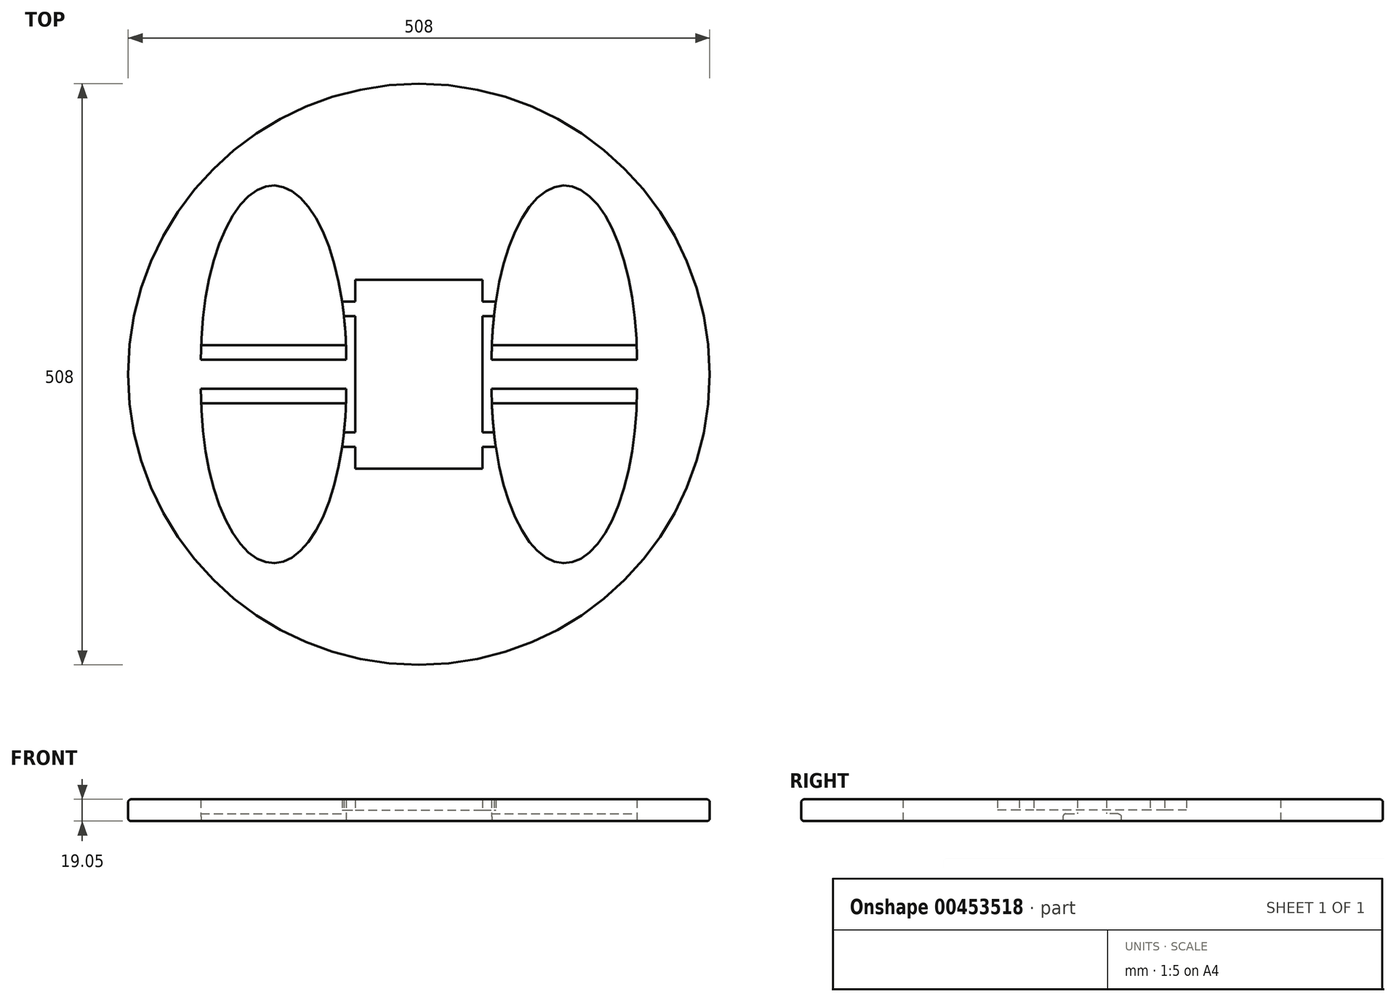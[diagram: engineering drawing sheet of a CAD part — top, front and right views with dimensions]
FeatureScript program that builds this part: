
annotation { "Feature Type Name" : "Feature", "Feature Type Description" : "" }
export const myFeature = defineFeature(function(context is Context, id is Id, definition is map)
    precondition{}
    {
        {
            var Q0;
            Q0=qCreatedBy(makeId("Top.planeOp"),FACE);
            var sketch = newSketch(context, id + "F0", { "sketchPlane" : qUnion([Q0])});
            skCircle(sketch, "E0", {"center": v(0, 0) * mm, "radius": 254 * mm});
            skLineSegment(sketch, "E1", {"start": v(-254, 0) * mm, "end": v(254, 0) * mm});
            skLineSegment(sketch, "E2", {"start": v(0, 254) * mm, "end": v(0, -254) * mm});
            skEllipticalArc(sketch, "E3", {});
            skEllipticalArc(sketch, "E4", {});
            skLineSegment(sketch, "E5", {"start": v(-190.5, 12.7) * mm, "end": v(-63.5, 12.7) * mm});
            skEllipticalArc(sketch, "E6.MirrorCS", {});
            skEllipticalArc(sketch, "E7.MirrorCS", {});
            skLineSegment(sketch, "E8.MirrorCS", {"start": v(-190.5, -12.7) * mm, "end": v(-63.5, -12.7) * mm});
            skLineSegment(sketch, "E9.trimOffspring", {"start": v(63.5, 12.7) * mm, "end": v(190.5, 12.7) * mm});
            skLineSegment(sketch, "E10.trimOffspring", {"start": v(63.5, -12.7) * mm, "end": v(190.5, -12.7) * mm});
            skLineSegment(sketch, "E11.0", {"start": v(-190.5, 25.4) * mm, "end": v(-63.5, 25.4) * mm});
            skLineSegment(sketch, "E12.0", {"start": v(63.5, 25.4) * mm, "end": v(190.5, 25.4) * mm});
            skLineSegment(sketch, "E13.0", {"start": v(63.5, -25.4) * mm, "end": v(190.5, -25.4) * mm});
            skLineSegment(sketch, "E14.0", {"start": v(-190.5, -25.4) * mm, "end": v(-63.5, -25.4) * mm});
            const initialGuessF0  = {"E3": [-0.127, 0.0127, 0, -1, 0.1524, 0.0635, 1.5707963267948966, 4.71238898038469], "E4": [0.127, 0.0127, 0, -1, 0.1524, 0.0635, 1.5707963267948966, 4.71238898038469], "E6.MirrorCS": [-0.127, -0.0127, 0, 1, 0.1524, 0.0635, 1.5707963267948966, 4.71238898038469], "E7.MirrorCS": [0.127, -0.0127, 0, 1, 0.1524, 0.0635, 1.5707963267948966, 4.71238898038469]};
            skSetInitialGuess(sketch, initialGuessF0);
            skSolve(sketch);
        }
        {
            var Q0;
            Q0 = qSketchRegion(id + "F0", true);
            extrude(context, id + "F1", {"entities" : qUnion([Q0]), "depth" : 19.05 * mm});
        }
        {
            var Q0;
            {var subQ0=sQuery(id+"F0.wireOp",EDGE,"E9.trimOffspring");Q0=makeQuery(id+"F0.imprint","IMPRINT",FACE,{"disambiguationData":[TD([[makeQuery(id+"F0.imprint","IMPRINT",EDGE,{"derivedFrom":subQ0}),1.0]])]});}
            var Q1;
            {var subQ0=sQuery(id+"F0.wireOp",EDGE,"E10.trimOffspring");Q1=makeQuery(id+"F0.imprint","IMPRINT",FACE,{"disambiguationData":[TD([[makeQuery(id+"F0.imprint","IMPRINT",EDGE,{"derivedFrom":subQ0}),-1.0]])]});}
            var Q2;
            {var subQ0=sQuery(id+"F0.wireOp",EDGE,"E8.MirrorCS");Q2=makeQuery(id+"F0.imprint","IMPRINT",FACE,{"disambiguationData":[TD([[makeQuery(id+"F0.imprint","IMPRINT",EDGE,{"derivedFrom":subQ0}),-1.0]])]});}
            var Q3;
            {var subQ0=sQuery(id+"F0.wireOp",EDGE,"E5");Q3=makeQuery(id+"F0.imprint","IMPRINT",FACE,{"disambiguationData":[TD([[makeQuery(id+"F0.imprint","IMPRINT",EDGE,{"derivedFrom":subQ0}),1.0]])]});}
            extrude(context, id + "F2", {"entities" : qUnion([Q0, Q1, Q2, Q3]), "operationType" : NewBodyOperationType.ADD, "depth" : 6.35 * mm});
        }
        {
            var Q0;
            Q0=qCreatedBy(makeId("Top.planeOp"),FACE);
            var sketch = newSketch(context, id + "F3", { "sketchPlane" : qUnion([Q0])});
            skLineSegment(sketch, "E15.bottom", {"start": v(-55.56, 82.55) * mm, "end": v(55.56, 82.55) * mm});
            skLineSegment(sketch, "E15.top", {"start": v(-55.56, -82.55) * mm, "end": v(55.56, -82.55) * mm});
            skLineSegment(sketch, "E15.left", {"start": v(-55.56, 82.55) * mm, "end": v(-55.56, -82.55) * mm});
            skLineSegment(sketch, "E15.right", {"start": v(55.56, 82.55) * mm, "end": v(55.56, -82.55) * mm});
            skPoint(sketch, "E15.middle", {"position": v(0, 0) * mm});
            skLineSegment(sketch, "E16.bottom", {"start": v(-101.6, 50.8) * mm, "end": v(101.6, 50.8) * mm});
            skLineSegment(sketch, "E16.top", {"start": v(-101.6, 63.5) * mm, "end": v(101.6, 63.5) * mm});
            skLineSegment(sketch, "E16.left", {"start": v(-101.6, 50.8) * mm, "end": v(-101.6, 63.5) * mm});
            skLineSegment(sketch, "E16.right", {"start": v(101.6, 50.8) * mm, "end": v(101.6, 63.5) * mm});
            skPoint(sketch, "E16.middle", {"position": v(0, 57.15) * mm});
            skLineSegment(sketch, "E17", {"start": v(0, 0) * mm, "end": v(55.56, 0) * mm});
            skLineSegment(sketch, "E18.MirrorCS", {"start": v(101.6, -50.8) * mm, "end": v(101.6, -63.5) * mm});
            skLineSegment(sketch, "E19.MirrorCS", {"start": v(-101.6, -50.8) * mm, "end": v(101.6, -50.8) * mm});
            skLineSegment(sketch, "E20.MirrorCS", {"start": v(-101.6, -63.5) * mm, "end": v(101.6, -63.5) * mm});
            skPoint(sketch, "E21.MirrorP", {"position": v(0, -57.15) * mm});
            skLineSegment(sketch, "E22.MirrorCS", {"start": v(-101.6, -50.8) * mm, "end": v(-101.6, -63.5) * mm});
            skLineSegment(sketch, "E23.MirrorCS", {"start": v(55.56, -82.55) * mm, "end": v(55.56, 82.55) * mm});
            skLineSegment(sketch, "E24.MirrorCS", {"start": v(-55.56, -82.55) * mm, "end": v(-55.56, 82.55) * mm});
            skSolve(sketch);
        }
        {
            var Q0;
            Q0=makeQuery(id+"F1.opExtrude","CAP_EDGE",EDGE,{"disambiguationData":[OSD([sQuery(id+"F0.wireOp",EDGE,"E0")])],"isStart":false});
            var Q1;
            {var subQ0=sQuery(id+"F3.wireOp",EDGE,"E24.MirrorCS");Q1=makeQuery(id+"FQuXiqpqz5MnNok_1.boolean.opBoolean","INTERSECT",EDGE,{"derivedFrom":[makeQuery(id+"F1.opExtrude","CAP_FACE",FACE,{"disambiguationData":[OSD([sQuery(id+"F0.wireOp",EDGE,"E0"),sQuery(id+"F0.wireOp",EDGE,"E3"),sQuery(id+"F0.wireOp",EDGE,"E4"),sQuery(id+"F0.wireOp",EDGE,"E5"),sQuery(id+"F0.wireOp",EDGE,"E6.MirrorCS"),sQuery(id+"F0.wireOp",EDGE,"E7.MirrorCS"),sQuery(id+"F0.wireOp",EDGE,"E8.MirrorCS"),sQuery(id+"F0.wireOp",EDGE,"E9.trimOffspring"),sQuery(id+"F0.wireOp",EDGE,"E10.trimOffspring")])],"isStart":false}),makeQuery(id+"FQuXiqpqz5MnNok_1.opExtrude","SWEPT_FACE",FACE,{"disambiguationData":[OSD([subQ0]),TDD([makeQuery(id+"F3.imprint","IMPRINT",EDGE,{"disambiguationData":[TD([[makeQuery(id+"F3.imprint","INTERSECT",VERTEX,{"derivedFrom":[sQuery(id+"F3.wireOp",EDGE,"E16.bottom"),subQ0]}),1.0]])],"derivedFrom":subQ0})])]})]});}
            var Q2;
            {var subQ0=sQuery(id+"F3.wireOp",EDGE,"E23.MirrorCS");var subQ1=makeQuery(id+"F3.imprint","IMPRINT",VERTEX,{"derivedFrom":subQ0});Q2=makeQuery(id+"FQuXiqpqz5MnNok_1.boolean.opBoolean","INTERSECT",EDGE,{"derivedFrom":[makeQuery(id+"F1.opExtrude","CAP_FACE",FACE,{"disambiguationData":[OSD([sQuery(id+"F0.wireOp",EDGE,"E0"),sQuery(id+"F0.wireOp",EDGE,"E3"),sQuery(id+"F0.wireOp",EDGE,"E4"),sQuery(id+"F0.wireOp",EDGE,"E5"),sQuery(id+"F0.wireOp",EDGE,"E6.MirrorCS"),sQuery(id+"F0.wireOp",EDGE,"E7.MirrorCS"),sQuery(id+"F0.wireOp",EDGE,"E8.MirrorCS"),sQuery(id+"F0.wireOp",EDGE,"E9.trimOffspring"),sQuery(id+"F0.wireOp",EDGE,"E10.trimOffspring")])],"isStart":false}),makeQuery(id+"FQuXiqpqz5MnNok_1.opExtrude","SWEPT_FACE",FACE,{"disambiguationData":[OSD([subQ0]),TDD([makeQuery(id+"F3.imprint","IMPRINT",EDGE,{"disambiguationData":[TD([[subQ1,1.0]])],"derivedFrom":subQ0}),makeQuery(id+"F3.imprint","IMPRINT",EDGE,{"disambiguationData":[TD([[subQ1,-1.0]])],"derivedFrom":subQ0})])]})]});}
            var Q3;
            Q3=makeQuery(id+"FQuXiqpqz5MnNok_1.boolean.opBoolean","INTERSECT",EDGE,{"derivedFrom":[makeQuery(id+"F1.opExtrude","CAP_FACE",FACE,{"disambiguationData":[OSD([sQuery(id+"F0.wireOp",EDGE,"E0"),sQuery(id+"F0.wireOp",EDGE,"E3"),sQuery(id+"F0.wireOp",EDGE,"E4"),sQuery(id+"F0.wireOp",EDGE,"E5"),sQuery(id+"F0.wireOp",EDGE,"E6.MirrorCS"),sQuery(id+"F0.wireOp",EDGE,"E7.MirrorCS"),sQuery(id+"F0.wireOp",EDGE,"E8.MirrorCS"),sQuery(id+"F0.wireOp",EDGE,"E9.trimOffspring"),sQuery(id+"F0.wireOp",EDGE,"E10.trimOffspring")])],"isStart":false}),makeQuery(id+"FQuXiqpqz5MnNok_1.opExtrude","SWEPT_FACE",FACE,{"disambiguationData":[OSD([sQuery(id+"F3.wireOp",EDGE,"E15.bottom")])]})]});
            var Q4;
            {var subQ0=sQuery(id+"F3.wireOp",EDGE,"E23.MirrorCS");Q4=makeQuery(id+"FQuXiqpqz5MnNok_1.boolean.opBoolean","INTERSECT",EDGE,{"derivedFrom":[makeQuery(id+"F1.opExtrude","CAP_FACE",FACE,{"disambiguationData":[OSD([sQuery(id+"F0.wireOp",EDGE,"E0"),sQuery(id+"F0.wireOp",EDGE,"E3"),sQuery(id+"F0.wireOp",EDGE,"E4"),sQuery(id+"F0.wireOp",EDGE,"E5"),sQuery(id+"F0.wireOp",EDGE,"E6.MirrorCS"),sQuery(id+"F0.wireOp",EDGE,"E7.MirrorCS"),sQuery(id+"F0.wireOp",EDGE,"E8.MirrorCS"),sQuery(id+"F0.wireOp",EDGE,"E9.trimOffspring"),sQuery(id+"F0.wireOp",EDGE,"E10.trimOffspring")])],"isStart":false}),makeQuery(id+"FQuXiqpqz5MnNok_1.opExtrude","SWEPT_FACE",FACE,{"disambiguationData":[OSD([subQ0]),TDD([makeQuery(id+"F3.imprint","IMPRINT",EDGE,{"disambiguationData":[TD([[makeQuery(id+"F3.imprint","INTERSECT",VERTEX,{"derivedFrom":[sQuery(id+"F3.wireOp",EDGE,"E15.bottom"),subQ0]}),1.0]])],"derivedFrom":subQ0})])]})]});}
            var Q5;
            {var subQ0=sQuery(id+"F3.wireOp",EDGE,"E24.MirrorCS");Q5=makeQuery(id+"FQuXiqpqz5MnNok_1.boolean.opBoolean","INTERSECT",EDGE,{"derivedFrom":[makeQuery(id+"F1.opExtrude","CAP_FACE",FACE,{"disambiguationData":[OSD([sQuery(id+"F0.wireOp",EDGE,"E0"),sQuery(id+"F0.wireOp",EDGE,"E3"),sQuery(id+"F0.wireOp",EDGE,"E4"),sQuery(id+"F0.wireOp",EDGE,"E5"),sQuery(id+"F0.wireOp",EDGE,"E6.MirrorCS"),sQuery(id+"F0.wireOp",EDGE,"E7.MirrorCS"),sQuery(id+"F0.wireOp",EDGE,"E8.MirrorCS"),sQuery(id+"F0.wireOp",EDGE,"E9.trimOffspring"),sQuery(id+"F0.wireOp",EDGE,"E10.trimOffspring")])],"isStart":false}),makeQuery(id+"FQuXiqpqz5MnNok_1.opExtrude","SWEPT_FACE",FACE,{"disambiguationData":[OSD([subQ0]),TDD([makeQuery(id+"F3.imprint","IMPRINT",EDGE,{"disambiguationData":[TD([[makeQuery(id+"F3.imprint","INTERSECT",VERTEX,{"derivedFrom":[sQuery(id+"F3.wireOp",EDGE,"E15.bottom"),subQ0]}),1.0]])],"derivedFrom":subQ0})])]})]});}
            var Q6;
            Q6=makeQuery(id+"FQuXiqpqz5MnNok_1.boolean.opBoolean","INTERSECT",EDGE,{"derivedFrom":[makeQuery(id+"F1.opExtrude","CAP_FACE",FACE,{"disambiguationData":[OSD([sQuery(id+"F0.wireOp",EDGE,"E0"),sQuery(id+"F0.wireOp",EDGE,"E3"),sQuery(id+"F0.wireOp",EDGE,"E4"),sQuery(id+"F0.wireOp",EDGE,"E5"),sQuery(id+"F0.wireOp",EDGE,"E6.MirrorCS"),sQuery(id+"F0.wireOp",EDGE,"E7.MirrorCS"),sQuery(id+"F0.wireOp",EDGE,"E8.MirrorCS"),sQuery(id+"F0.wireOp",EDGE,"E9.trimOffspring"),sQuery(id+"F0.wireOp",EDGE,"E10.trimOffspring")])],"isStart":false}),makeQuery(id+"FQuXiqpqz5MnNok_1.opExtrude","SWEPT_FACE",FACE,{"disambiguationData":[OSD([sQuery(id+"F3.wireOp",EDGE,"E15.top")])]})]});
            var Q7;
            {var subQ0=sQuery(id+"F3.wireOp",EDGE,"E23.MirrorCS");Q7=makeQuery(id+"FQuXiqpqz5MnNok_1.boolean.opBoolean","INTERSECT",EDGE,{"derivedFrom":[makeQuery(id+"F1.opExtrude","CAP_FACE",FACE,{"disambiguationData":[OSD([sQuery(id+"F0.wireOp",EDGE,"E0"),sQuery(id+"F0.wireOp",EDGE,"E3"),sQuery(id+"F0.wireOp",EDGE,"E4"),sQuery(id+"F0.wireOp",EDGE,"E5"),sQuery(id+"F0.wireOp",EDGE,"E6.MirrorCS"),sQuery(id+"F0.wireOp",EDGE,"E7.MirrorCS"),sQuery(id+"F0.wireOp",EDGE,"E8.MirrorCS"),sQuery(id+"F0.wireOp",EDGE,"E9.trimOffspring"),sQuery(id+"F0.wireOp",EDGE,"E10.trimOffspring")])],"isStart":false}),makeQuery(id+"FQuXiqpqz5MnNok_1.opExtrude","SWEPT_FACE",FACE,{"disambiguationData":[OSD([subQ0]),TDD([makeQuery(id+"F3.imprint","IMPRINT",EDGE,{"disambiguationData":[TD([[makeQuery(id+"F3.imprint","INTERSECT",VERTEX,{"derivedFrom":[sQuery(id+"F3.wireOp",EDGE,"E15.top"),subQ0]}),-1.0]])],"derivedFrom":subQ0})])]})]});}
            var Q8;
            {var subQ0=sQuery(id+"F3.wireOp",EDGE,"E24.MirrorCS");Q8=makeQuery(id+"FQuXiqpqz5MnNok_1.boolean.opBoolean","INTERSECT",EDGE,{"derivedFrom":[makeQuery(id+"F1.opExtrude","CAP_FACE",FACE,{"disambiguationData":[OSD([sQuery(id+"F0.wireOp",EDGE,"E0"),sQuery(id+"F0.wireOp",EDGE,"E3"),sQuery(id+"F0.wireOp",EDGE,"E4"),sQuery(id+"F0.wireOp",EDGE,"E5"),sQuery(id+"F0.wireOp",EDGE,"E6.MirrorCS"),sQuery(id+"F0.wireOp",EDGE,"E7.MirrorCS"),sQuery(id+"F0.wireOp",EDGE,"E8.MirrorCS"),sQuery(id+"F0.wireOp",EDGE,"E9.trimOffspring"),sQuery(id+"F0.wireOp",EDGE,"E10.trimOffspring")])],"isStart":false}),makeQuery(id+"FQuXiqpqz5MnNok_1.opExtrude","SWEPT_FACE",FACE,{"disambiguationData":[OSD([subQ0]),TDD([makeQuery(id+"F3.imprint","IMPRINT",EDGE,{"disambiguationData":[TD([[makeQuery(id+"F3.imprint","INTERSECT",VERTEX,{"derivedFrom":[sQuery(id+"F3.wireOp",EDGE,"E15.top"),subQ0]}),-1.0]])],"derivedFrom":subQ0})])]})]});}
            var Q9;
            Q9=makeQuery(id+"F2.opExtrude","CAP_EDGE",EDGE,{"disambiguationData":[OSD([sQuery(id+"F0.wireOp",EDGE,"E14.0")])],"isStart":false});
            var Q10;
            Q10=makeQuery(id+"F2.opExtrude","CAP_EDGE",EDGE,{"disambiguationData":[OSD([sQuery(id+"F0.wireOp",EDGE,"E13.0")])],"isStart":false});
            var Q11;
            Q11=makeQuery(id+"F2.opExtrude","CAP_EDGE",EDGE,{"disambiguationData":[OSD([sQuery(id+"F0.wireOp",EDGE,"E12.0")])],"isStart":false});
            var Q12;
            Q12=makeQuery(id+"F2.opExtrude","CAP_EDGE",EDGE,{"disambiguationData":[OSD([sQuery(id+"F0.wireOp",EDGE,"E11.0")])],"isStart":false});
            fillet(context, id + "F4", {"entities" : qUnion([Q0, Q1, Q2, Q3, Q4, Q5, Q6, Q7, Q8, Q9, Q10, Q11, Q12]), "radius" : 2.54 * mm, "tangentPropagation" : true, "allowEdgeOverflow" : false});
        }
        {
            var Q0;
            Q0 = qSketchRegion(id + "F3", true);
            extrude(context, id + "F5", {"entities" : qUnion([Q0]), "operationType" : NewBodyOperationType.REMOVE, "depth" : 19.05 * mm, "offsetDistance" : 25.4 * mm, "hasSecondDirection" : true, "secondDirectionOppositeDirection" : false, "secondDirectionDepth" : 9.52 * mm});
        }
        {
            var Q0;
            Q0=makeQuery(id+"F1.opExtrude","CAP_EDGE",EDGE,{"disambiguationData":[OSD([sQuery(id+"F0.wireOp",EDGE,"E0")])],"isStart":true});
            fillet(context, id + "F6", {"entities" : qUnion([Q0]), "radius" : 2.54 * mm, "tangentPropagation" : true, "allowEdgeOverflow" : false});
        }
    });
